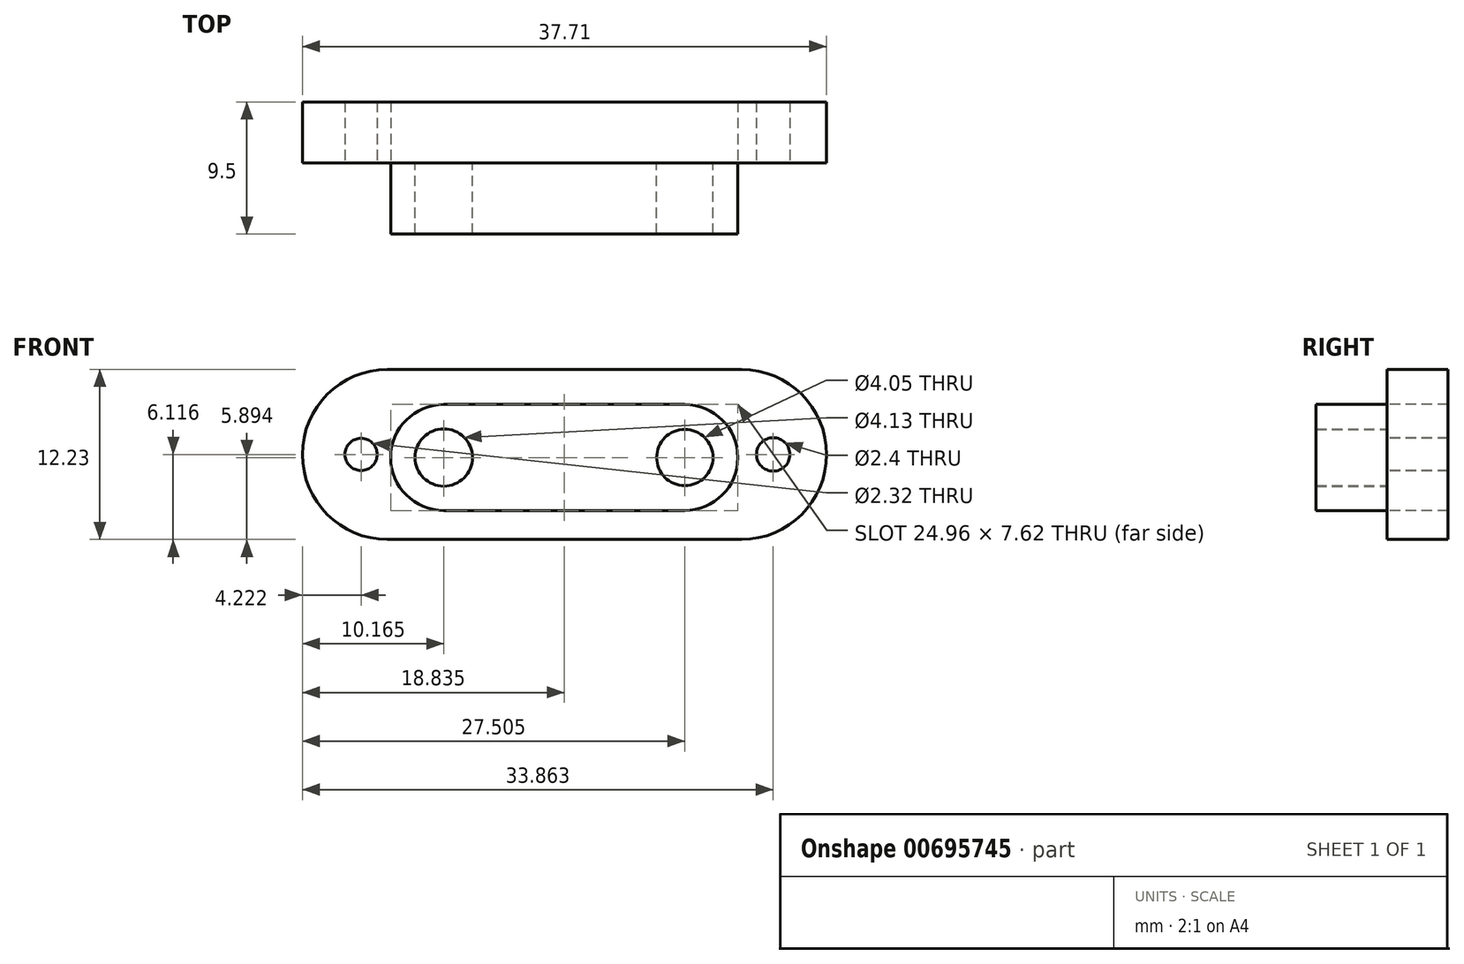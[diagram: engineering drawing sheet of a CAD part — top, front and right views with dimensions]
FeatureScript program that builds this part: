
annotation { "Feature Type Name" : "Feature", "Feature Type Description" : "" }
export const myFeature = defineFeature(function(context is Context, id is Id, definition is map)
    precondition{}
    {
        {
            var Q0;
            Q0=qCreatedBy(makeId("Front.planeOp"),FACE);
            var sketch = newSketch(context, id + "F0", { "sketchPlane" : qUnion([Q0])});
            skLineSegment(sketch, "E0", {"start": v(0, 0) * mm, "end": v(-25.47, 0) * mm});
            skLineSegment(sketch, "E1", {"start": v(0, 12.23) * mm, "end": v(-25.47, 12.23) * mm});
            skArc(sketch, "E2", {"start": v(-25.47, 12.23) * mm, "mid": v(-31.59, 6.12) * mm, "end": v(-25.47, 0) * mm});
            skArc(sketch, "E3", {"start": v(0, 0) * mm, "mid": v(6.12, 6.12) * mm, "end": v(0, 12.23) * mm});
            skLineSegment(sketch, "E4", {"start": v(-21.43, 2.08) * mm, "end": v(-4.08, 2.08) * mm});
            skLineSegment(sketch, "E5", {"start": v(-21.43, 9.7) * mm, "end": v(-4.08, 9.7) * mm});
            skPoint(sketch, "E6.end.orphan", {"position": v(-4.08, 9.7) * mm});
            skPoint(sketch, "E7.orphan", {"position": v(0, 9.7) * mm});
            skPoint(sketch, "E8.end.orphan", {"position": v(-4.08, 2.08) * mm});
            skPoint(sketch, "E9.orphan", {"position": v(0, 2.08) * mm});
            skPoint(sketch, "E10.end.orphan", {"position": v(-21.43, 2.08) * mm});
            skPoint(sketch, "E11.end.orphan", {"position": v(-21.43, 9.7) * mm});
            skArc(sketch, "E12", {"start": v(-21.43, 9.7) * mm, "mid": v(-25.24, 5.9) * mm, "end": v(-21.43, 2.08) * mm});
            skArc(sketch, "E13", {"start": v(-4.08, 2.08) * mm, "mid": v(-0.27, 5.9) * mm, "end": v(-4.08, 9.7) * mm});
            skCircle(sketch, "E14", {"center": v(-4.08, 5.9) * mm, "radius": 2.03 * mm});
            skCircle(sketch, "E15", {"center": v(-21.43, 5.9) * mm, "radius": 2.06 * mm});
            skCircle(sketch, "E16", {"center": v(2.27, 6.12) * mm, "radius": 1.2 * mm});
            skCircle(sketch, "E17", {"center": v(-27.37, 6.12) * mm, "radius": 1.16 * mm});
            skSolve(sketch);
        }
        {
            var Q0;
            Q0 = qSketchRegion(id + "F0", true);
            extrude(context, id + "F1", {"entities" : qUnion([Q0]), "oppositeDirection" : true, "depth" : 4.4 * mm, "offsetDistance" : 25 * mm});
        }
        {
            var Q0;
            Q0=makeQuery(id+"F0.imprint","IMPRINT",FACE,{"disambiguationData":[TD([[makeQuery(id+"F0.imprint","IMPRINT",EDGE,{"derivedFrom":sQuery(id+"F0.wireOp",EDGE,"E4")}),1.0]])]});
            extrude(context, id + "F2", {"entities" : qUnion([Q0]), "depth" : 5.1 * mm, "offsetDistance" : 25 * mm});
        }
    });
